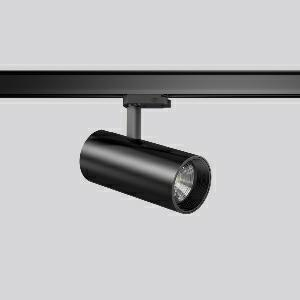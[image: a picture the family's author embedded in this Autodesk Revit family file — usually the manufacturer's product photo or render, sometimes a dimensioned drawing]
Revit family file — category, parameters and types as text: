
# Revit family: deecos_s_mini_742206_003_2_76_f181
name_source: partatom
category: Lighting Fixtures
units: mm (PartAtom-declared; Revit-internal decimal feet)

## family parameters
Cut with Voids When Loaded = No
Host = Face
Light Source = No
Part Type = Normal
Room Calculation Point = No
Round Connector Dimension = Use Diameter
Shared = No

## types (1)
- DEECOS S mini (1 x LED Modul 927, 3000 lm, 2700)
    Apparent Load = 29 VA
    Approval mark = CE
    CIE Flux Codes = 99 100 100 100 100
    Color Rendering = 92
    Color Temperature = 2700
    Default Elevation = 1800 mm
    Description = Series: DEECOS S mini
LED surface-mounted projector in modern design with no visible cooling ribs. Housing: die-cast aluminium, powder-coated. Rotation range: 356°. Swivel range: 90°. Black plastic ring and recessed LED to prevent glare from the side. Optical assembly with lens made of plastic (polycarbonate) for the best homogeneous light distribution - can be changed without tools. Best colour rendering index Ra>90. With adapter for RZB 3-circuit DALI tracks. Suitable for Track on ceiling, Wall track. High quality converter without flickering and stroboscopic effect. The following accessories can be mounted without use of tools: interchangeable lenses, decorative glasses, honeycomb louvre, clear and frosted diffusers, white interchangeable plastic ring. 
Colour: deep black, matt (RAL 9005)
Diameter: 87 mm
Height: 214 mm
Lamp: LED
Socket: without socket
Colour temperature: 2700K
Colour rendering index (CRI): 92
System power: 29 W
Rated luminous flux: 3000 lm
Luminous efficiency: 103 lm/W
Control gear: Converter, dimmable, DALI
Protection class: I
Type of protection: IP 20
    Height = 214 mm
    Lamp = 1 x LED Modul 927
    Lamp Light Flux = 3000 lm
    Lamp count = 1
    Length = 87 mm
    Lifetime = 50000 h
    Luminous efficacy = 103 lm/W
    Manufacturer = RZB
    ModVariant = No
    Model = 742206.003.2.76
    Mounting Place = Ceiling
    Mounting Type = Rail mounted
    Number of Poles = 1
    OnlyDefault = Yes
    Power Factor = 1
    Product Name = DEECOS S mini
    Product group = Track mounted projectors
    ProductGroupID = 301
    Protection Class = Protection class I
    Protection Degree = IP 20
    RLX_Detail_Level = 1
    RLX_Emergency_Light_Flux = 0 lm
    RLX_Emergency_Type = 0
    RLX_Emergency_Type_DB = No
    RlxData = <blob elided: 38557 chars, md5=8cd08b4f>
    Socket = socket
    Standby Power = 0 W
    System Light Flux = 3000 lm
    System Power = 29 W
    Type Comments = Product without accessories
    Type Image = 741930.003.jpg
    URL = http://relux.com
    VarID = ---
    Voltage = 230 V
    Voltage Range = 220-240 V
    Weight = 0.00 kg
    Width = 0 mm  [stored 0 ft]

note: [stored X ft] marks values corroborated as IEEE doubles in the binary element streams (Revit-internal decimal feet)

## geometry (parser evidence)
native form markers: Blend x4, Sweep x12
no freeform markers — native parametric forms only
